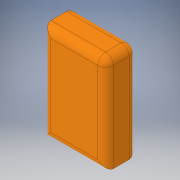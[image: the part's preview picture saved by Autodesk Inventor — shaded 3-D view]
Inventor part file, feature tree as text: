
AUTODESK INVENTOR PART (.ipt)
format: ipt  version: 2019 (Build 230136000, 136)  size: 109,056 bytes
history: native  units: in
note: dims shown in document units (in); Inventor stores cm internally (conversion verified against a paired STEP export)
features: extrude x1, fillet x1, sketch x1
ambient origin geometry x8: Origin, YZ Plane, XZ Plane, XY Plane, X Axis, Y Axis, Z Axis, Center Point
bodies: Solid1 (feature_tree)
feature tree (3):
  extrude  "Extrusion1"  Depth=0.25in TaperAngle=0.0deg
  fillet  "Fillet1"  Radius=0.0625in
  sketch  "Sketch1"  dims[d0=0.5in d1=0.25in d2=0.0in d3=0.0625in]
